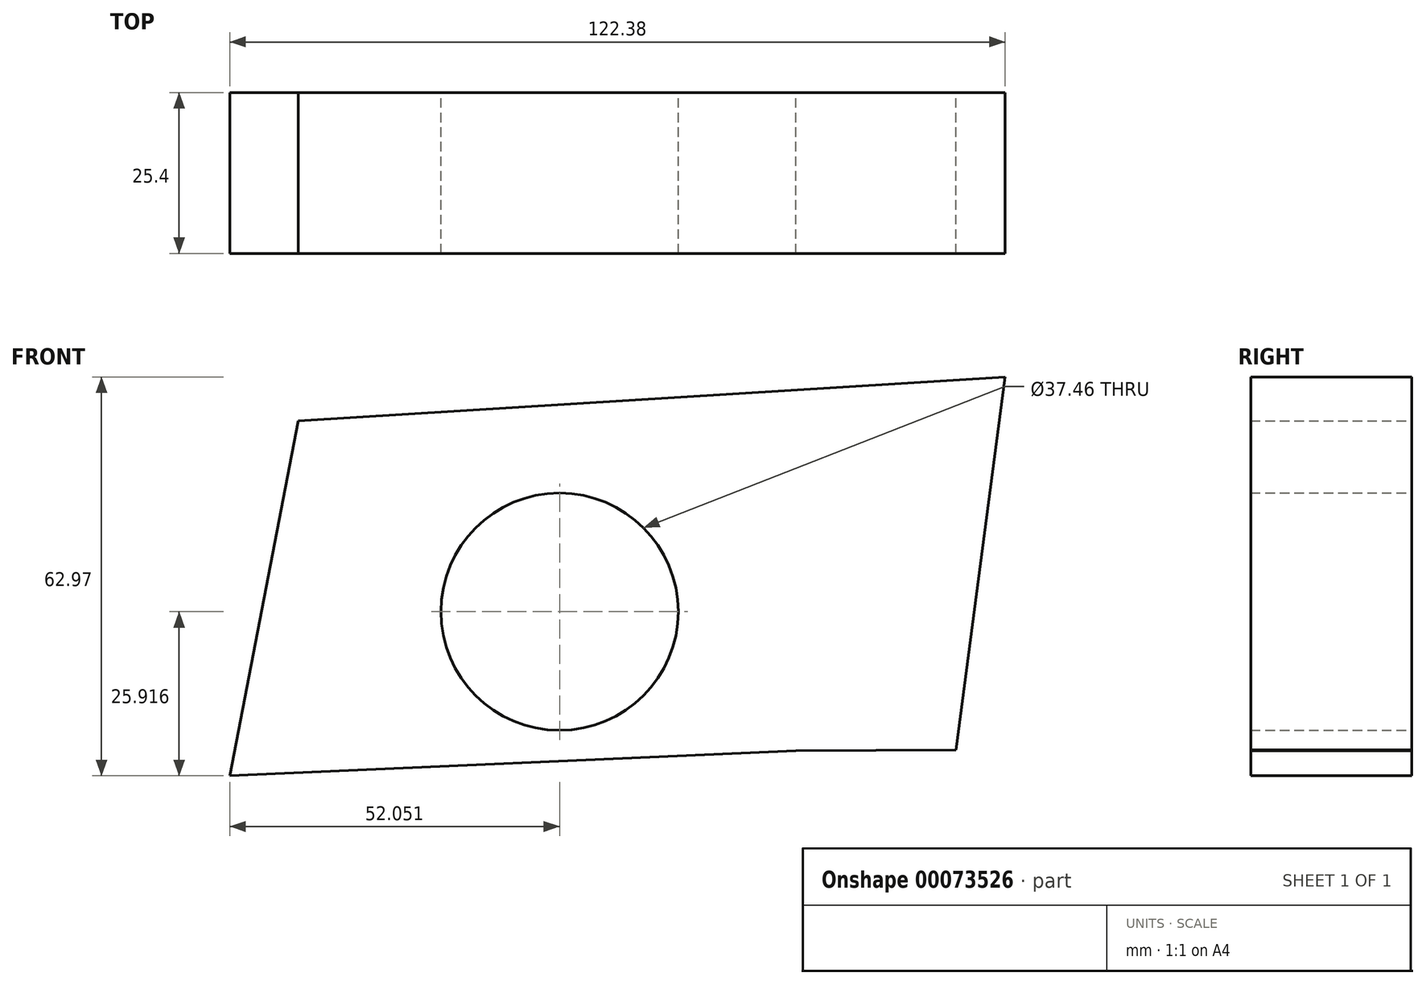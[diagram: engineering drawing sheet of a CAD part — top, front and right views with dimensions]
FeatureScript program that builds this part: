
annotation { "Feature Type Name" : "Feature", "Feature Type Description" : "" }
export const myFeature = defineFeature(function(context is Context, id is Id, definition is map)
    precondition{}
    {
        {
            var Q0;
            Q0=qCreatedBy(makeId("Front.planeOp"),FACE);
            var sketch = newSketch(context, id + "F0", { "sketchPlane" : qUnion([Q0])});
            skLineSegment(sketch, "E0", {"start": v(0, -4.12) * mm, "end": v(-89.34, -8.1) * mm});
            skLineSegment(sketch, "E1", {"start": v(-89.34, -8.1) * mm, "end": v(-78.55, 47.95) * mm});
            skLineSegment(sketch, "E2", {"start": v(-78.55, 47.95) * mm, "end": v(33.04, 54.88) * mm});
            skLineSegment(sketch, "E3", {"start": v(33.04, 54.88) * mm, "end": v(25.28, -4) * mm});
            skLineSegment(sketch, "E4", {"start": v(25.28, -4) * mm, "end": v(0, -4.12) * mm});
            skLineSegment(sketch, "E5", {"start": v(-66.75, 43.27) * mm, "end": v(-49.57, 44.34) * mm});
            skLineSegment(sketch, "E6", {"start": v(-49.57, 44.34) * mm, "end": v(-50.57, 33.1) * mm});
            skLineSegment(sketch, "E7", {"start": v(-50.57, 33.1) * mm, "end": v(-70.12, 27.46) * mm});
            skLineSegment(sketch, "E8", {"start": v(-70.12, 27.46) * mm, "end": v(-67.09, 42.83) * mm});
            skLineSegment(sketch, "E9", {"start": v(-14.83, 44.34) * mm, "end": v(3.47, 45.47) * mm});
            skLineSegment(sketch, "E10", {"start": v(3.47, 45.47) * mm, "end": v(1.35, 26.52) * mm});
            skLineSegment(sketch, "E11", {"start": v(1.35, 26.52) * mm, "end": v(-20.9, 26.52) * mm});
            skLineSegment(sketch, "E12", {"start": v(-20.9, 26.52) * mm, "end": v(-15.5, 43.56) * mm});
            skSolve(sketch);
        }
        {
            var Q0;
            Q0 = qSketchRegion(id + "F0", true);
            extrude(context, id + "F1", {"entities" : qUnion([Q0]), "depth" : 25.4 * mm});
        }
        {
            var Q0;
            Q0=makeQuery(id+"F1.opExtrude","CAP_FACE",FACE,{"disambiguationData":[OSD([sQuery(id+"F0.wireOp",EDGE,"E0"),sQuery(id+"F0.wireOp",EDGE,"E1"),sQuery(id+"F0.wireOp",EDGE,"E2"),sQuery(id+"F0.wireOp",EDGE,"E3"),sQuery(id+"F0.wireOp",EDGE,"E4")])],"isStart":true});
            var sketch = newSketch(context, id + "F2", { "sketchPlane" : qUnion([Q0])});
            skCircle(sketch, "E13", {"center": v(37.29, 17.83) * mm, "radius": 18.73 * mm});
            skSolve(sketch);
        }
        {
            var Q0;
            Q0 = qSketchRegion(id + "F2", true);
            extrude(context, id + "F3", {"entities" : qUnion([Q0]), "operationType" : NewBodyOperationType.REMOVE, "oppositeDirection" : true, "depth" : 25.4 * mm});
        }
    });
